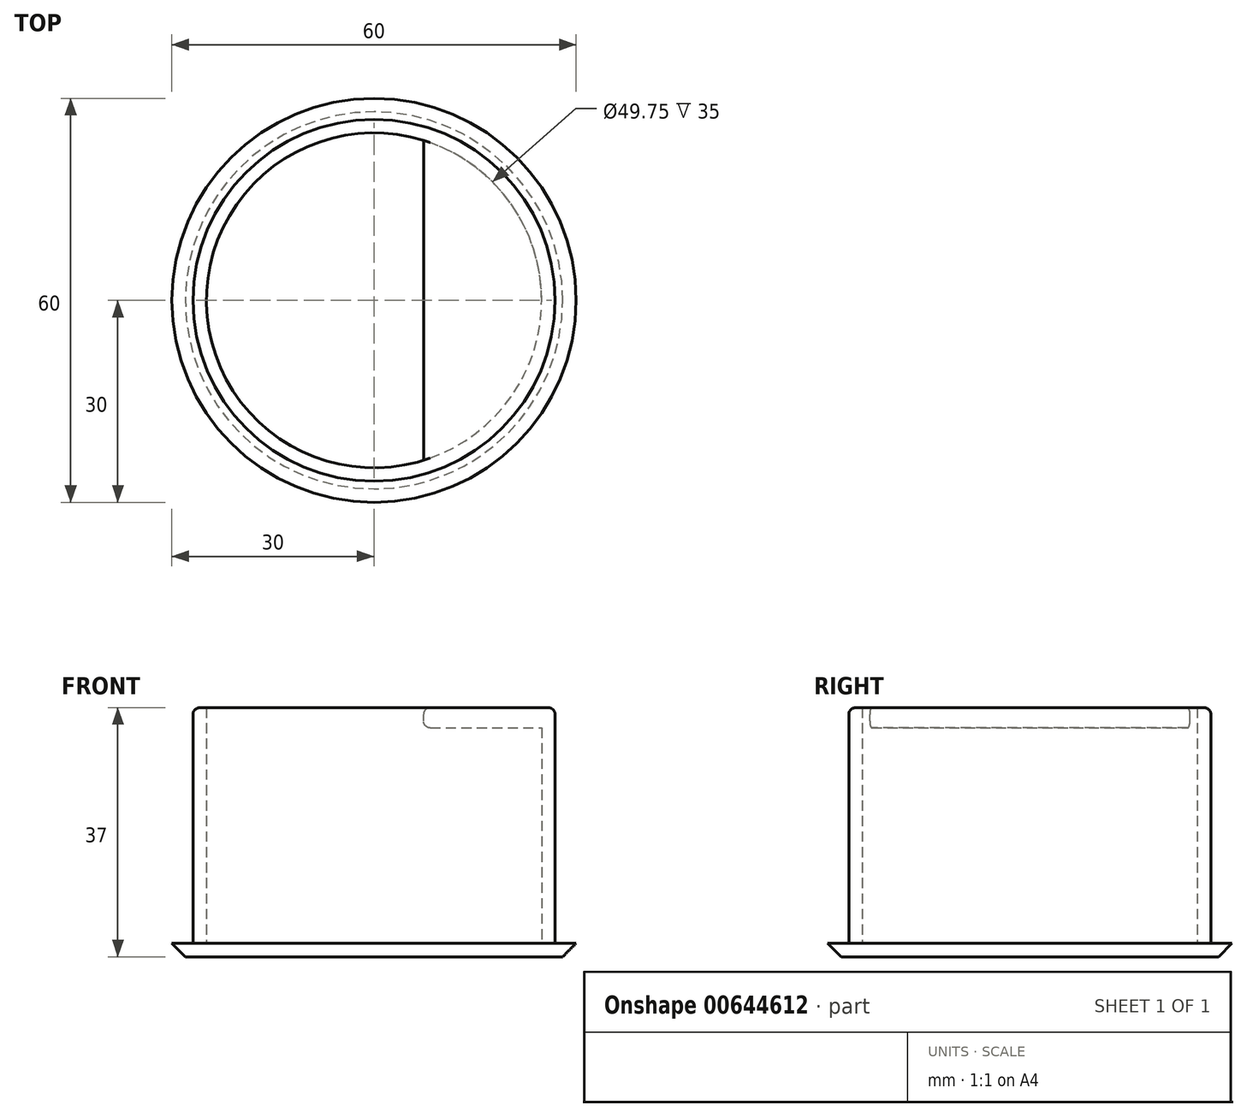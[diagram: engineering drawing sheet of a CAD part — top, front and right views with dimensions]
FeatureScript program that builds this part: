
annotation { "Feature Type Name" : "Feature", "Feature Type Description" : "" }
export const myFeature = defineFeature(function(context is Context, id is Id, definition is map)
    precondition{}
    {
        {
            var Q0;
            Q0=qCreatedBy(makeId("Top.planeOp"),FACE);
            var sketch = newSketch(context, id + "F0", { "sketchPlane" : qUnion([Q0])});
            skCircle(sketch, "E0", {"center": v(0, 0) * mm, "radius": 26.88 * mm});
            skCircle(sketch, "E1", {"center": v(0, 0) * mm, "radius": 30 * mm});
            skCircle(sketch, "E2.0", {"center": v(0, 0) * mm, "radius": 24.88 * mm});
            skSolve(sketch);
        }
        {
            var Q0;
            Q0=makeQuery(id+"F0.imprint","IMPRINT",FACE,{"disambiguationData":[TD([[makeQuery(id+"F0.imprint","IMPRINT",EDGE,{"derivedFrom":sQuery(id+"F0.wireOp",EDGE,"E0")}),1.0]])]});
            extrude(context, id + "F1", {"entities" : qUnion([Q0]), "depth" : 37 * mm, "offsetDistance" : 25 * mm});
        }
        {
            var Q0;
            Q0=makeQuery(id+"F0.imprint","IMPRINT",FACE,{"disambiguationData":[TD([[makeQuery(id+"F0.imprint","IMPRINT",EDGE,{"derivedFrom":sQuery(id+"F0.wireOp",EDGE,"E0")}),-1.0]])]});
            var Q1;
            Q1=makeQuery(id+"F0.imprint","IMPRINT",FACE,{"disambiguationData":[TD([[makeQuery(id+"F0.imprint","IMPRINT",EDGE,{"derivedFrom":sQuery(id+"F0.wireOp",EDGE,"E2.0")}),1.0]])]});
            extrude(context, id + "F2", {"entities" : qUnion([Q0, Q1]), "operationType" : NewBodyOperationType.ADD, "depth" : 2 * mm, "offsetDistance" : 25 * mm});
        }
        {
            var Q0;
            Q0=makeQuery(id+"F1.opExtrude","CAP_FACE",FACE,{"disambiguationData":[OSD([sQuery(id+"F0.wireOp",EDGE,"E0"),sQuery(id+"F0.wireOp",EDGE,"E2.0")])],"isStart":false});
            var sketch = newSketch(context, id + "F3", { "sketchPlane" : qUnion([Q0])});
            skCircle(sketch, "E3.0", {"center": v(0, 0) * mm, "radius": 24.88 * mm});
            skCircle(sketch, "E3.1", {"center": v(0, 0) * mm, "radius": 24.88 * mm});
            skLineSegment(sketch, "E4", {"start": v(7.36, 23.76) * mm, "end": v(7.36, -23.76) * mm});
            skSolve(sketch);
        }
        {
            var Q0;
            {var subQ0=sQuery(id+"F3.wireOp",EDGE,"E4");Q0=makeQuery(id+"F3.imprint","IMPRINT",FACE,{"disambiguationData":[TD([[makeQuery(id+"F3.imprint","IMPRINT",EDGE,{"derivedFrom":subQ0}),1.0]])]});}
            extrude(context, id + "F4", {"entities" : qUnion([Q0]), "operationType" : NewBodyOperationType.ADD, "oppositeDirection" : true, "depth" : 3 * mm, "offsetDistance" : 25 * mm});
        }
        {
            var Q0;
            Q0=makeQuery(id+"F4.opExtrude","CAP_EDGE",EDGE,{"disambiguationData":[OSD([sQuery(id+"F3.wireOp",EDGE,"E4")])],"isStart":false});
            var Q1;
            Q1=makeQuery(id+"F4.opExtrude","CAP_EDGE",EDGE,{"disambiguationData":[OSD([sQuery(id+"F3.wireOp",EDGE,"E4")])],"isStart":true});
            var Q2;
            Q2=makeQuery(id+"F1.opExtrude","CAP_EDGE",EDGE,{"disambiguationData":[OSD([sQuery(id+"F0.wireOp",EDGE,"E0")])],"isStart":false});
            fillet(context, id + "F5", {"entities" : qUnion([Q0, Q1, Q2]), "radius" : 1 * mm, "tangentPropagation" : true, "allowEdgeOverflow" : false});
        }
        {
            var Q0;
            Q0=makeQuery(id+"F2.opExtrude","CAP_EDGE",EDGE,{"disambiguationData":[OSD([sQuery(id+"F0.wireOp",EDGE,"E1")])],"isStart":true});
            chamfer(context, id + "F6", {"entities" : qUnion([Q0]), "width" : 2 * mm, "tangentPropagation" : true});
        }
    });
